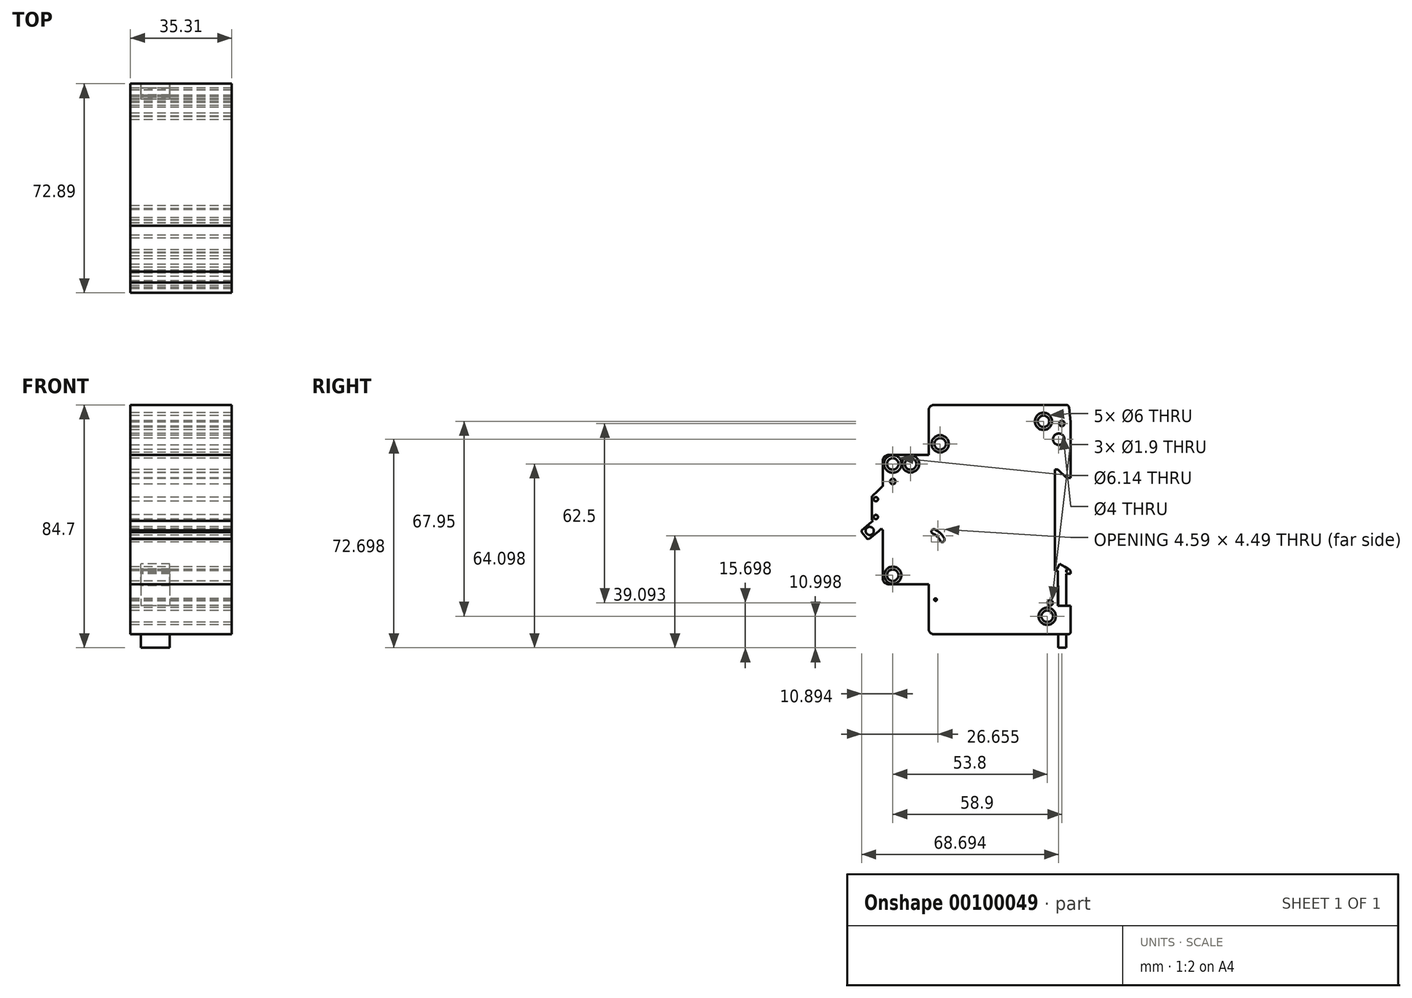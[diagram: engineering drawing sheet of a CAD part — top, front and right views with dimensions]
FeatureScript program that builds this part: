
annotation { "Feature Type Name" : "Feature", "Feature Type Description" : "" }
export const myFeature = defineFeature(function(context is Context, id is Id, definition is map)
    precondition{}
    {
        {
            var Q0;
            Q0=qCreatedBy(makeId("Right.planeOp"),FACE);
            var sketch = newSketch(context, id + "F0", { "sketchPlane" : qUnion([Q0])});
            skLineSegment(sketch, "E0", {"start": v(-13.7, -26.36) * mm, "end": v(-11.78, -28.67) * mm});
            skLineSegment(sketch, "E1", {"start": v(-13.64, -25.66) * mm, "end": v(-13.7, -26.36) * mm});
            skLineSegment(sketch, "E2", {"start": v(59.17, -40.86) * mm, "end": v(59.17, -40.36) * mm});
            skLineSegment(sketch, "E3", {"start": v(53.77, -39.11) * mm, "end": v(53.77, -39.76) * mm});
            skLineSegment(sketch, "E4", {"start": v(54.77, -38.39) * mm, "end": v(55.27, -37.36) * mm});
            skLineSegment(sketch, "E5", {"start": v(57.57, -40.86) * mm, "end": v(59.17, -40.86) * mm});
            skLineSegment(sketch, "E6", {"start": v(54.42, -39.11) * mm, "end": v(53.77, -39.11) * mm});
            skLineSegment(sketch, "E7", {"start": v(54.42, -39.11) * mm, "end": v(54.77, -38.39) * mm});
            skLineSegment(sketch, "E8", {"start": v(58.52, -39.24) * mm, "end": v(57.07, -38.4) * mm});
            skLineSegment(sketch, "E9", {"start": v(57.07, -38.4) * mm, "end": v(55.27, -37.36) * mm});
            skLineSegment(sketch, "E10", {"start": v(-10.26, -22.84) * mm, "end": v(-7.7, -25.9) * mm});
            skLineSegment(sketch, "E11", {"start": v(-11.78, -28.67) * mm, "end": v(-11.07, -28.73) * mm});
            skLineSegment(sketch, "E12", {"start": v(-7.7, -25.9) * mm, "end": v(-11.07, -28.73) * mm});
            skLineSegment(sketch, "E13", {"start": v(59.2, 12.04) * mm, "end": v(59.2, -7.46) * mm});
            skLineSegment(sketch, "E14", {"start": v(59.2, 12.04) * mm, "end": v(58.57, 17.16) * mm});
            skLineSegment(sketch, "E15", {"start": v(59.2, -7.46) * mm, "end": v(57.7, -7.46) * mm});
            skLineSegment(sketch, "E16", {"start": v(9.7, -59.96) * mm, "end": v(9.7, -44.46) * mm});
            skLineSegment(sketch, "E17", {"start": v(-9.98, -25.2) * mm, "end": v(-9.83, -25.39) * mm});
            skLineSegment(sketch, "E18", {"start": v(-10.13, -25.03) * mm, "end": v(-9.98, -25.2) * mm});
            skLineSegment(sketch, "E19", {"start": v(-9.74, -22.4) * mm, "end": v(-9.94, -22.21) * mm});
            skLineSegment(sketch, "E20", {"start": v(-10.1, -21.84) * mm, "end": v(-10.1, -14.08) * mm});
            skLineSegment(sketch, "E21", {"start": v(-8.1, -23.9) * mm, "end": v(-9.74, -22.4) * mm});
            skLineSegment(sketch, "E22", {"start": v(-10.26, -22.84) * mm, "end": v(-9.74, -22.4) * mm});
            skLineSegment(sketch, "E23", {"start": v(-9.94, -13.71) * mm, "end": v(-8.1, -12.02) * mm});
            skLineSegment(sketch, "E24", {"start": v(-13.64, -25.66) * mm, "end": v(-10.26, -22.84) * mm});
            skLineSegment(sketch, "E25", {"start": v(-8.1, -12.02) * mm, "end": v(-7.5, -11.47) * mm});
            skLineSegment(sketch, "E26", {"start": v(-7.5, -11.47) * mm, "end": v(-6.47, -10.51) * mm});
            skLineSegment(sketch, "E27", {"start": v(53.7, -4.46) * mm, "end": v(53.7, -39.76) * mm});
            skLineSegment(sketch, "E28", {"start": v(-7.5, -24.46) * mm, "end": v(-7.5, -11.47) * mm});
            skLineSegment(sketch, "E29", {"start": v(-8.1, -15.31) * mm, "end": v(-8.1, -20.61) * mm});
            skLineSegment(sketch, "E30", {"start": v(-8.1, -12.02) * mm, "end": v(-8.1, -14.41) * mm});
            skLineSegment(sketch, "E31", {"start": v(53.7, -4.46) * mm, "end": v(54.7, -4.46) * mm});
            skLineSegment(sketch, "E32", {"start": v(57.7, -7.46) * mm, "end": v(54.7, -4.46) * mm});
            skLineSegment(sketch, "E33", {"start": v(11.7, 18.04) * mm, "end": v(57.57, 18.04) * mm});
            skLineSegment(sketch, "E34", {"start": v(9.7, 0.54) * mm, "end": v(9.7, 16.04) * mm});
            skLineSegment(sketch, "E35", {"start": v(-6.3, -1.46) * mm, "end": v(-6.3, -10.14) * mm});
            skLineSegment(sketch, "E36", {"start": v(-4.3, 0.54) * mm, "end": v(9.7, 0.54) * mm});
            skLineSegment(sketch, "E37", {"start": v(54.77, -61.96) * mm, "end": v(54.77, -66.66) * mm});
            skLineSegment(sketch, "E38", {"start": v(57.57, -66.66) * mm, "end": v(57.57, -61.96) * mm});
            skLineSegment(sketch, "E39", {"start": v(54.77, -66.66) * mm, "end": v(57.57, -66.66) * mm});
            skLineSegment(sketch, "E40", {"start": v(54.77, -51.96) * mm, "end": v(59.2, -51.96) * mm});
            skLineSegment(sketch, "E41", {"start": v(59.2, -51.96) * mm, "end": v(59.2, -60.96) * mm});
            skLineSegment(sketch, "E42", {"start": v(58.2, -61.96) * mm, "end": v(11.7, -61.96) * mm});
            skLineSegment(sketch, "E43", {"start": v(53.7, -39.76) * mm, "end": v(53.77, -39.76) * mm});
            skLineSegment(sketch, "E44", {"start": v(53.77, -39.76) * mm, "end": v(54.4, -39.76) * mm});
            skLineSegment(sketch, "E45", {"start": v(54.77, -44.96) * mm, "end": v(54.77, -47.16) * mm});
            skLineSegment(sketch, "E46", {"start": v(54.7, -44.96) * mm, "end": v(54.7, -40.06) * mm});
            skLineSegment(sketch, "E47", {"start": v(57.57, -40.86) * mm, "end": v(57.57, -47.16) * mm});
            skLineSegment(sketch, "E48", {"start": v(54.77, -44.96) * mm, "end": v(54.7, -44.96) * mm});
            skLineSegment(sketch, "E49", {"start": v(57.57, -39.46) * mm, "end": v(57.57, -40.26) * mm});
            skLineSegment(sketch, "E50", {"start": v(54.7, -51.96) * mm, "end": v(54.77, -51.96) * mm});
            skLineSegment(sketch, "E51", {"start": v(57.57, -47.16) * mm, "end": v(57.57, -51.96) * mm});
            skLineSegment(sketch, "E52", {"start": v(54.77, -51.96) * mm, "end": v(54.77, -47.16) * mm});
            skLineSegment(sketch, "E53", {"start": v(54.7, -51.96) * mm, "end": v(54.7, -44.96) * mm});
            skLineSegment(sketch, "E54", {"start": v(9.7, -44.46) * mm, "end": v(-4.3, -44.46) * mm});
            skLineSegment(sketch, "E55", {"start": v(-8.1, -21.51) * mm, "end": v(-8.1, -23.9) * mm});
            skLineSegment(sketch, "E56", {"start": v(-6.47, -25.41) * mm, "end": v(-6.77, -25.13) * mm});
            skLineSegment(sketch, "E57", {"start": v(-6.77, -25.13) * mm, "end": v(-7.5, -24.46) * mm});
            skLineSegment(sketch, "E58", {"start": v(-8.97, -21.76) * mm, "end": v(-7.97, -20.92) * mm});
            skLineSegment(sketch, "E59", {"start": v(-7.5, -24.46) * mm, "end": v(-8.1, -23.9) * mm});
            skLineSegment(sketch, "E60", {"start": v(-6.3, -42.46) * mm, "end": v(-6.3, -25.78) * mm});
            skLineSegment(sketch, "E61", {"start": v(-6.77, -25.13) * mm, "end": v(-7.7, -25.9) * mm});
            skArc(sketch, "E62", {"start": v(59.17, -40.36) * mm, "mid": v(59, -39.71) * mm, "end": v(58.52, -39.24) * mm});
            skArc(sketch, "E63", {"start": v(-10.13, -25.03) * mm, "mid": v(-11.89, -25.55) * mm, "end": v(-10.82, -27.04) * mm});
            skArc(sketch, "E64", {"start": v(-10.82, -27.04) * mm, "mid": v(-9.86, -26.5) * mm, "end": v(-9.83, -25.39) * mm});
            skArc(sketch, "E65", {"start": v(9.7, -59.96) * mm, "mid": v(10.28, -61.38) * mm, "end": v(11.7, -61.96) * mm});
            skArc(sketch, "E66", {"start": v(-9.83, -25.39) * mm, "mid": v(-9.96, -25.2) * mm, "end": v(-10.13, -25.03) * mm});
            skArc(sketch, "E67", {"start": v(-10.1, -21.84) * mm, "mid": v(-10.06, -22.04) * mm, "end": v(-9.94, -22.21) * mm});
            skArc(sketch, "E68", {"start": v(-9.94, -13.71) * mm, "mid": v(-10.06, -13.88) * mm, "end": v(-10.1, -14.08) * mm});
            skArc(sketch, "E69", {"start": v(11.7, 18.04) * mm, "mid": v(10.28, 17.45) * mm, "end": v(9.7, 16.04) * mm});
            skArc(sketch, "E70", {"start": v(-6.47, -10.51) * mm, "mid": v(-6.35, -10.34) * mm, "end": v(-6.3, -10.14) * mm});
            skArc(sketch, "E71", {"start": v(-8.1, -15.31) * mm, "mid": v(-7.96, -14.86) * mm, "end": v(-8.1, -14.41) * mm});
            skArc(sketch, "E72", {"start": v(-8.1, -14.41) * mm, "mid": v(-9.46, -14.86) * mm, "end": v(-8.1, -15.31) * mm});
            skArc(sketch, "E73", {"start": v(58.57, 17.16) * mm, "mid": v(58.24, 17.79) * mm, "end": v(57.57, 18.04) * mm});
            skArc(sketch, "E74", {"start": v(-4.3, 0.54) * mm, "mid": v(-5.72, -0.05) * mm, "end": v(-6.3, -1.46) * mm});
            skArc(sketch, "E75", {"start": v(58.2, -61.96) * mm, "mid": v(58.9, -61.67) * mm, "end": v(59.2, -60.96) * mm});
            skArc(sketch, "E76", {"start": v(57.77, -39.86) * mm, "mid": v(57.72, -39.64) * mm, "end": v(57.57, -39.46) * mm});
            skArc(sketch, "E77", {"start": v(57.57, -40.26) * mm, "mid": v(57.72, -40.09) * mm, "end": v(57.77, -39.86) * mm});
            skArc(sketch, "E78", {"start": v(54.7, -40.06) * mm, "mid": v(54.6, -39.85) * mm, "end": v(54.4, -39.76) * mm});
            skArc(sketch, "E79", {"start": v(-6.3, -42.46) * mm, "mid": v(-5.72, -43.88) * mm, "end": v(-4.3, -44.46) * mm});
            skArc(sketch, "E80", {"start": v(15.18, -28.67) * mm, "mid": v(13.78, -26.71) * mm, "end": v(11.77, -25.39) * mm});
            skArc(sketch, "E81", {"start": v(-8.97, -21.76) * mm, "mid": v(-8.5, -21.78) * mm, "end": v(-8.1, -21.51) * mm});
            skArc(sketch, "E82", {"start": v(-7.97, -20.92) * mm, "mid": v(-8.02, -20.76) * mm, "end": v(-8.1, -20.61) * mm});
            skArc(sketch, "E83", {"start": v(-8.1, -21.51) * mm, "mid": v(-7.98, -21.23) * mm, "end": v(-7.97, -20.92) * mm});
            skArc(sketch, "E84", {"start": v(-8.1, -20.61) * mm, "mid": v(-9.3, -20.61) * mm, "end": v(-8.97, -21.76) * mm});
            skArc(sketch, "E85", {"start": v(-6.3, -25.78) * mm, "mid": v(-6.35, -25.58) * mm, "end": v(-6.47, -25.41) * mm});
            skArc(sketch, "E86", {"start": v(11.77, -25.39) * mm, "mid": v(10.72, -25.81) * mm, "end": v(11.15, -26.86) * mm});
            skArc(sketch, "E87", {"start": v(13.73, -29.35) * mm, "mid": v(14.79, -29.74) * mm, "end": v(15.18, -28.67) * mm});
            skArc(sketch, "E88", {"start": v(13.73, -29.35) * mm, "mid": v(12.67, -27.87) * mm, "end": v(11.15, -26.86) * mm});
            skCircle(sketch, "E89", {"center": v(48.2, -37.86) * mm, "radius": 2 * mm});
            skCircle(sketch, "E90", {"center": v(48.2, -37.86) * mm, "radius": 3 * mm});
            skCircle(sketch, "E91", {"center": v(-10.82, -25.91) * mm, "radius": 1.1 * mm});
            skCircle(sketch, "E92", {"center": v(-10.82, -25.91) * mm, "radius": 0.7 * mm});
            skCircle(sketch, "E93", {"center": v(-10.82, -25.91) * mm, "radius": 1.42 * mm});
            skCircle(sketch, "E94", {"center": v(48.2, -37.86) * mm, "radius": 0.55 * mm});
            skCircle(sketch, "E95", {"center": v(48.2, -37.86) * mm, "radius": 1.65 * mm});
            skCircle(sketch, "E96", {"center": v(56.1, 11.54) * mm, "radius": 0.95 * mm});
            skCircle(sketch, "E97", {"center": v(55, 6.04) * mm, "radius": 2 * mm});
            skCircle(sketch, "E98", {"center": v(49.7, 12.29) * mm, "radius": 0.55 * mm});
            skCircle(sketch, "E99", {"center": v(49.7, 12.29) * mm, "radius": 1.65 * mm});
            skCircle(sketch, "E100", {"center": v(49.7, 12.29) * mm, "radius": 2 * mm});
            skCircle(sketch, "E101", {"center": v(49.7, 12.29) * mm, "radius": 3 * mm});
            skCircle(sketch, "E102", {"center": v(13.7, 4.44) * mm, "radius": 0.55 * mm});
            skCircle(sketch, "E103", {"center": v(13.7, 4.44) * mm, "radius": 1.65 * mm});
            skCircle(sketch, "E104", {"center": v(-2.8, -8.66) * mm, "radius": 0.95 * mm});
            skCircle(sketch, "E105", {"center": v(-2.8, -2.56) * mm, "radius": 0.55 * mm});
            skCircle(sketch, "E106", {"center": v(-2.8, -2.56) * mm, "radius": 1.65 * mm});
            skCircle(sketch, "E107", {"center": v(3.4, -2.56) * mm, "radius": 0.55 * mm});
            skCircle(sketch, "E108", {"center": v(3.4, -2.56) * mm, "radius": 1.65 * mm});
            skCircle(sketch, "E109", {"center": v(13.7, 4.44) * mm, "radius": 2 * mm});
            skCircle(sketch, "E110", {"center": v(-2.8, -2.56) * mm, "radius": 2 * mm});
            skCircle(sketch, "E111", {"center": v(3.4, -2.56) * mm, "radius": 2 * mm});
            skCircle(sketch, "E112", {"center": v(13.7, 4.44) * mm, "radius": 3 * mm});
            skCircle(sketch, "E113", {"center": v(3.4, -2.56) * mm, "radius": 3 * mm});
            skCircle(sketch, "E114", {"center": v(-2.8, -2.56) * mm, "radius": 3.07 * mm});
            skCircle(sketch, "E115", {"center": v(51, -55.66) * mm, "radius": 0.55 * mm});
            skCircle(sketch, "E116", {"center": v(52, -50.96) * mm, "radius": 0.95 * mm});
            skCircle(sketch, "E117", {"center": v(51, -55.66) * mm, "radius": 1.65 * mm});
            skCircle(sketch, "E118", {"center": v(51, -55.66) * mm, "radius": 2 * mm});
            skCircle(sketch, "E119", {"center": v(51, -55.66) * mm, "radius": 3 * mm});
            skCircle(sketch, "E120", {"center": v(-2.8, -41.36) * mm, "radius": 1.82 * mm});
            skCircle(sketch, "E121", {"center": v(12.1, -49.86) * mm, "radius": 1.5 * mm});
            skCircle(sketch, "E122", {"center": v(12.1, -49.86) * mm, "radius": 1.7 * mm});
            skCircle(sketch, "E123", {"center": v(12.1, -49.86) * mm, "radius": 0.45 * mm});
            skCircle(sketch, "E124", {"center": v(-2.8, -41.36) * mm, "radius": 2 * mm});
            skCircle(sketch, "E125", {"center": v(-2.8, -41.36) * mm, "radius": 3 * mm});
            skSolve(sketch);
        }
        {
            var Q0;
            Q0=makeQuery(id+"F0.imprint","IMPRINT",FACE,{"disambiguationData":[TD([[makeQuery(id+"F0.imprint","IMPRINT",EDGE,{"derivedFrom":sQuery(id+"F0.wireOp",EDGE,"E13")}),-1.0]])]});
            var Q1;
            Q1=makeQuery(id+"F0.imprint","IMPRINT",FACE,{"disambiguationData":[TD([[makeQuery(id+"F0.imprint","IMPRINT",EDGE,{"derivedFrom":sQuery(id+"F0.wireOp",EDGE,"E110")}),1.0]])]});
            var Q2;
            Q2=makeQuery(id+"F0.imprint","IMPRINT",FACE,{"disambiguationData":[TD([[makeQuery(id+"F0.imprint","IMPRINT",EDGE,{"derivedFrom":sQuery(id+"F0.wireOp",EDGE,"E111")}),1.0]])]});
            var Q3;
            Q3=makeQuery(id+"F0.imprint","IMPRINT",FACE,{"disambiguationData":[TD([[makeQuery(id+"F0.imprint","IMPRINT",EDGE,{"derivedFrom":sQuery(id+"F0.wireOp",EDGE,"E104")}),-1.0]])]});
            var Q4;
            Q4=makeQuery(id+"F0.imprint","IMPRINT",FACE,{"disambiguationData":[TD([[makeQuery(id+"F0.imprint","IMPRINT",EDGE,{"derivedFrom":sQuery(id+"F0.wireOp",EDGE,"E106")}),1.0]])]});
            var Q5;
            Q5=makeQuery(id+"F0.imprint","IMPRINT",FACE,{"disambiguationData":[TD([[makeQuery(id+"F0.imprint","IMPRINT",EDGE,{"derivedFrom":sQuery(id+"F0.wireOp",EDGE,"E105")}),1.0]])]});
            var Q6;
            Q6=makeQuery(id+"F0.imprint","IMPRINT",FACE,{"disambiguationData":[TD([[makeQuery(id+"F0.imprint","IMPRINT",EDGE,{"derivedFrom":sQuery(id+"F0.wireOp",EDGE,"E105")}),-1.0]])]});
            var Q7;
            Q7=makeQuery(id+"F0.imprint","IMPRINT",FACE,{"disambiguationData":[TD([[makeQuery(id+"F0.imprint","IMPRINT",EDGE,{"derivedFrom":sQuery(id+"F0.wireOp",EDGE,"E108")}),1.0]])]});
            var Q8;
            Q8=makeQuery(id+"F0.imprint","IMPRINT",FACE,{"disambiguationData":[TD([[makeQuery(id+"F0.imprint","IMPRINT",EDGE,{"derivedFrom":sQuery(id+"F0.wireOp",EDGE,"E107")}),1.0]])]});
            var Q9;
            Q9=makeQuery(id+"F0.imprint","IMPRINT",FACE,{"disambiguationData":[TD([[makeQuery(id+"F0.imprint","IMPRINT",EDGE,{"derivedFrom":sQuery(id+"F0.wireOp",EDGE,"E107")}),-1.0]])]});
            var Q10;
            Q10=makeQuery(id+"F0.imprint","IMPRINT",FACE,{"disambiguationData":[TD([[makeQuery(id+"F0.imprint","IMPRINT",EDGE,{"derivedFrom":sQuery(id+"F0.wireOp",EDGE,"E109")}),1.0]])]});
            var Q11;
            Q11=makeQuery(id+"F0.imprint","IMPRINT",FACE,{"disambiguationData":[TD([[makeQuery(id+"F0.imprint","IMPRINT",EDGE,{"derivedFrom":sQuery(id+"F0.wireOp",EDGE,"E103")}),1.0]])]});
            var Q12;
            Q12=makeQuery(id+"F0.imprint","IMPRINT",FACE,{"disambiguationData":[TD([[makeQuery(id+"F0.imprint","IMPRINT",EDGE,{"derivedFrom":sQuery(id+"F0.wireOp",EDGE,"E102")}),1.0]])]});
            var Q13;
            Q13=makeQuery(id+"F0.imprint","IMPRINT",FACE,{"disambiguationData":[TD([[makeQuery(id+"F0.imprint","IMPRINT",EDGE,{"derivedFrom":sQuery(id+"F0.wireOp",EDGE,"E102")}),-1.0]])]});
            var Q14;
            Q14=makeQuery(id+"F0.imprint","IMPRINT",FACE,{"disambiguationData":[TD([[makeQuery(id+"F0.imprint","IMPRINT",EDGE,{"derivedFrom":sQuery(id+"F0.wireOp",EDGE,"E100")}),1.0]])]});
            var Q15;
            Q15=makeQuery(id+"F0.imprint","IMPRINT",FACE,{"disambiguationData":[TD([[makeQuery(id+"F0.imprint","IMPRINT",EDGE,{"derivedFrom":sQuery(id+"F0.wireOp",EDGE,"E99")}),1.0]])]});
            var Q16;
            Q16=makeQuery(id+"F0.imprint","IMPRINT",FACE,{"disambiguationData":[TD([[makeQuery(id+"F0.imprint","IMPRINT",EDGE,{"derivedFrom":sQuery(id+"F0.wireOp",EDGE,"E98")}),1.0]])]});
            var Q17;
            Q17=makeQuery(id+"F0.imprint","IMPRINT",FACE,{"disambiguationData":[TD([[makeQuery(id+"F0.imprint","IMPRINT",EDGE,{"derivedFrom":sQuery(id+"F0.wireOp",EDGE,"E98")}),-1.0]])]});
            var Q18;
            Q18=makeQuery(id+"F0.imprint","IMPRINT",FACE,{"disambiguationData":[TD([[makeQuery(id+"F0.imprint","IMPRINT",EDGE,{"derivedFrom":sQuery(id+"F0.wireOp",EDGE,"E96")}),-1.0]])]});
            var Q19;
            Q19=makeQuery(id+"F0.imprint","IMPRINT",FACE,{"disambiguationData":[TD([[makeQuery(id+"F0.imprint","IMPRINT",EDGE,{"derivedFrom":sQuery(id+"F0.wireOp",EDGE,"E97")}),-1.0]])]});
            var Q20;
            Q20=makeQuery(id+"F0.imprint","IMPRINT",FACE,{"disambiguationData":[TD([[makeQuery(id+"F0.imprint","IMPRINT",EDGE,{"derivedFrom":sQuery(id+"F0.wireOp",EDGE,"E89")}),1.0]])]});
            var Q21;
            Q21=makeQuery(id+"F0.imprint","IMPRINT",FACE,{"disambiguationData":[TD([[makeQuery(id+"F0.imprint","IMPRINT",EDGE,{"derivedFrom":sQuery(id+"F0.wireOp",EDGE,"E89")}),-1.0]])]});
            var Q22;
            Q22=makeQuery(id+"F0.imprint","IMPRINT",FACE,{"disambiguationData":[TD([[makeQuery(id+"F0.imprint","IMPRINT",EDGE,{"derivedFrom":sQuery(id+"F0.wireOp",EDGE,"E94")}),1.0]])]});
            var Q23;
            Q23=makeQuery(id+"F0.imprint","IMPRINT",FACE,{"disambiguationData":[TD([[makeQuery(id+"F0.imprint","IMPRINT",EDGE,{"derivedFrom":sQuery(id+"F0.wireOp",EDGE,"E94")}),-1.0]])]});
            var Q24;
            Q24=makeQuery(id+"F0.imprint","IMPRINT",FACE,{"disambiguationData":[TD([[makeQuery(id+"F0.imprint","IMPRINT",EDGE,{"derivedFrom":sQuery(id+"F0.wireOp",EDGE,"E116")}),-1.0]])]});
            var Q25;
            Q25=makeQuery(id+"F0.imprint","IMPRINT",FACE,{"disambiguationData":[TD([[makeQuery(id+"F0.imprint","IMPRINT",EDGE,{"derivedFrom":sQuery(id+"F0.wireOp",EDGE,"E118")}),1.0]])]});
            var Q26;
            Q26=makeQuery(id+"F0.imprint","IMPRINT",FACE,{"disambiguationData":[TD([[makeQuery(id+"F0.imprint","IMPRINT",EDGE,{"derivedFrom":sQuery(id+"F0.wireOp",EDGE,"E117")}),1.0]])]});
            var Q27;
            Q27=makeQuery(id+"F0.imprint","IMPRINT",FACE,{"disambiguationData":[TD([[makeQuery(id+"F0.imprint","IMPRINT",EDGE,{"derivedFrom":sQuery(id+"F0.wireOp",EDGE,"E115")}),1.0]])]});
            var Q28;
            Q28=makeQuery(id+"F0.imprint","IMPRINT",FACE,{"disambiguationData":[TD([[makeQuery(id+"F0.imprint","IMPRINT",EDGE,{"derivedFrom":sQuery(id+"F0.wireOp",EDGE,"E115")}),-1.0]])]});
            var Q29;
            Q29=makeQuery(id+"F0.imprint","IMPRINT",FACE,{"disambiguationData":[TD([[makeQuery(id+"F0.imprint","IMPRINT",EDGE,{"derivedFrom":sQuery(id+"F0.wireOp",EDGE,"E121")}),1.0]])]});
            var Q30;
            Q30=makeQuery(id+"F0.imprint","IMPRINT",FACE,{"disambiguationData":[TD([[makeQuery(id+"F0.imprint","IMPRINT",EDGE,{"derivedFrom":sQuery(id+"F0.wireOp",EDGE,"E121")}),-1.0]])]});
            var Q31;
            Q31=makeQuery(id+"F0.imprint","IMPRINT",FACE,{"disambiguationData":[TD([[makeQuery(id+"F0.imprint","IMPRINT",EDGE,{"derivedFrom":sQuery(id+"F0.wireOp",EDGE,"E123")}),-1.0]])]});
            var Q32;
            Q32=makeQuery(id+"F0.imprint","IMPRINT",FACE,{"disambiguationData":[TD([[makeQuery(id+"F0.imprint","IMPRINT",EDGE,{"derivedFrom":sQuery(id+"F0.wireOp",EDGE,"E124")}),1.0]])]});
            var Q33;
            Q33=makeQuery(id+"F0.imprint","IMPRINT",FACE,{"disambiguationData":[TD([[makeQuery(id+"F0.imprint","IMPRINT",EDGE,{"derivedFrom":sQuery(id+"F0.wireOp",EDGE,"E120")}),1.0]])]});
            var Q34;
            Q34=makeQuery(id+"F0.imprint","IMPRINT",FACE,{"disambiguationData":[TD([[makeQuery(id+"F0.imprint","IMPRINT",EDGE,{"derivedFrom":sQuery(id+"F0.wireOp",EDGE,"E120")}),-1.0]])]});
            extrude(context, id + "F1", {"entities" : qUnion([Q0, Q1, Q2, Q3, Q4, Q5, Q6, Q7, Q8, Q9, Q10, Q11, Q12, Q13, Q14, Q15, Q16, Q17, Q18, Q19, Q20, Q21, Q22, Q23, Q24, Q25, Q26, Q27, Q28, Q29, Q30, Q31, Q32, Q33, Q34]), "depth" : 35.3 * mm});
        }
        {
            var Q0;
            Q0=makeQuery(id+"F0.imprint","IMPRINT",FACE,{"disambiguationData":[TD([[makeQuery(id+"F0.imprint","IMPRINT",EDGE,{"derivedFrom":sQuery(id+"F0.wireOp",EDGE,"E2")}),1.0]])]});
            var Q1;
            Q1=makeQuery(id+"F0.imprint","IMPRINT",FACE,{"disambiguationData":[TD([[makeQuery(id+"F0.imprint","IMPRINT",EDGE,{"derivedFrom":sQuery(id+"F0.wireOp",EDGE,"E4")}),-1.0]])]});
            var Q2;
            Q2=makeQuery(id+"F0.imprint","IMPRINT",FACE,{"disambiguationData":[TD([[makeQuery(id+"F0.imprint","IMPRINT",EDGE,{"derivedFrom":sQuery(id+"F0.wireOp",EDGE,"E3")}),1.0]])]});
            var Q3;
            Q3=makeQuery(id+"F0.imprint","IMPRINT",FACE,{"disambiguationData":[TD([[makeQuery(id+"F0.imprint","IMPRINT",EDGE,{"derivedFrom":sQuery(id+"F0.wireOp",EDGE,"86a625e0-e1d9-4c3e-84fe-78c421ad609b")}),1.0]])]});
            var Q4;
            {var subQ0=sQuery(id+"F0.wireOp",EDGE,"E37");Q4=makeQuery(id+"F0.imprint","IMPRINT",FACE,{"disambiguationData":[TD([[makeQuery(id+"F0.imprint","IMPRINT",EDGE,{"derivedFrom":subQ0}),1.0]])]});}
            extrude(context, id + "F2", {"entities" : qUnion([Q0, Q1, Q2, Q3, Q4]), "depth" : 13.7 * mm});
        }
        {
            var Q0;
            {var subQ0=sQuery(id+"F0.wireOp",EDGE,"E37");Q0=makeQuery(id+"F0.imprint","IMPRINT",FACE,{"disambiguationData":[TD([[makeQuery(id+"F0.imprint","IMPRINT",EDGE,{"derivedFrom":subQ0}),1.0]])]});}
            var Q1;
            Q1=makeQuery(id+"F0.imprint","IMPRINT",FACE,{"disambiguationData":[TD([[makeQuery(id+"F0.imprint","IMPRINT",EDGE,{"derivedFrom":sQuery(id+"F0.wireOp",EDGE,"E2")}),1.0]])]});
            extrude(context, id + "F3", {"entities" : qUnion([Q0, Q1]), "operationType" : NewBodyOperationType.REMOVE, "depth" : 3.7 * mm});
        }
        {
            var Q0;
            Q0=makeQuery(id+"F0.imprint","IMPRINT",FACE,{"disambiguationData":[TD([[makeQuery(id+"F0.imprint","IMPRINT",EDGE,{"derivedFrom":sQuery(id+"F0.wireOp",EDGE,"E0")}),1.0]])]});
            var Q1;
            Q1=makeQuery(id+"F0.imprint","IMPRINT",FACE,{"disambiguationData":[TD([[makeQuery(id+"F0.imprint","IMPRINT",EDGE,{"derivedFrom":sQuery(id+"F0.wireOp",EDGE,"E10")}),1.0]])]});
            var Q2;
            Q2=makeQuery(id+"F0.imprint","IMPRINT",FACE,{"disambiguationData":[TD([[makeQuery(id+"F0.imprint","IMPRINT",EDGE,{"derivedFrom":sQuery(id+"F0.wireOp",EDGE,"E19")}),-1.0]])]});
            var Q3;
            Q3=makeQuery(id+"F0.imprint","IMPRINT",FACE,{"disambiguationData":[TD([[makeQuery(id+"F0.imprint","IMPRINT",EDGE,{"derivedFrom":sQuery(id+"F0.wireOp",EDGE,"E25")}),-1.0]])]});
            var Q4;
            Q4=makeQuery(id+"F1.opExtrude","CAP_FACE",FACE,{"disambiguationData":[OSD([sQuery(id+"F0.wireOp",EDGE,"E13"),sQuery(id+"F0.wireOp",EDGE,"E14"),sQuery(id+"F0.wireOp",EDGE,"E15"),sQuery(id+"F0.wireOp",EDGE,"E16"),sQuery(id+"F0.wireOp",EDGE,"E26"),sQuery(id+"F0.wireOp",EDGE,"E27"),sQuery(id+"F0.wireOp",EDGE,"E28"),sQuery(id+"F0.wireOp",EDGE,"E31"),sQuery(id+"F0.wireOp",EDGE,"E32"),sQuery(id+"F0.wireOp",EDGE,"E33"),sQuery(id+"F0.wireOp",EDGE,"E34"),sQuery(id+"F0.wireOp",EDGE,"E35"),sQuery(id+"F0.wireOp",EDGE,"E36"),sQuery(id+"F0.wireOp",EDGE,"E40"),sQuery(id+"F0.wireOp",EDGE,"E41"),sQuery(id+"F0.wireOp",EDGE,"E42"),sQuery(id+"F0.wireOp",EDGE,"E43"),sQuery(id+"F0.wireOp",EDGE,"E44"),sQuery(id+"F0.wireOp",EDGE,"E46"),sQuery(id+"F0.wireOp",EDGE,"E50"),sQuery(id+"F0.wireOp",EDGE,"E53"),sQuery(id+"F0.wireOp",EDGE,"E54"),sQuery(id+"F0.wireOp",EDGE,"E56"),sQuery(id+"F0.wireOp",EDGE,"E57"),sQuery(id+"F0.wireOp",EDGE,"E60"),sQuery(id+"F0.wireOp",EDGE,"E65"),sQuery(id+"F0.wireOp",EDGE,"E69"),sQuery(id+"F0.wireOp",EDGE,"E70"),sQuery(id+"F0.wireOp",EDGE,"E73"),sQuery(id+"F0.wireOp",EDGE,"E74"),sQuery(id+"F0.wireOp",EDGE,"E75"),sQuery(id+"F0.wireOp",EDGE,"E78"),sQuery(id+"F0.wireOp",EDGE,"E79"),sQuery(id+"F0.wireOp",EDGE,"E80"),sQuery(id+"F0.wireOp",EDGE,"E85"),sQuery(id+"F0.wireOp",EDGE,"E86"),sQuery(id+"F0.wireOp",EDGE,"E87"),sQuery(id+"F0.wireOp",EDGE,"E88")])],"isStart":false});
            extrude(context, id + "F4", {"entities" : qUnion([Q0, Q1, Q2, Q3]), "operationType" : NewBodyOperationType.ADD, "endBound" : BoundingType.UP_TO_SURFACE, "endBoundEntityFace" : qUnion([Q4]), "depth" : 25.4 * mm});
        }
    });
